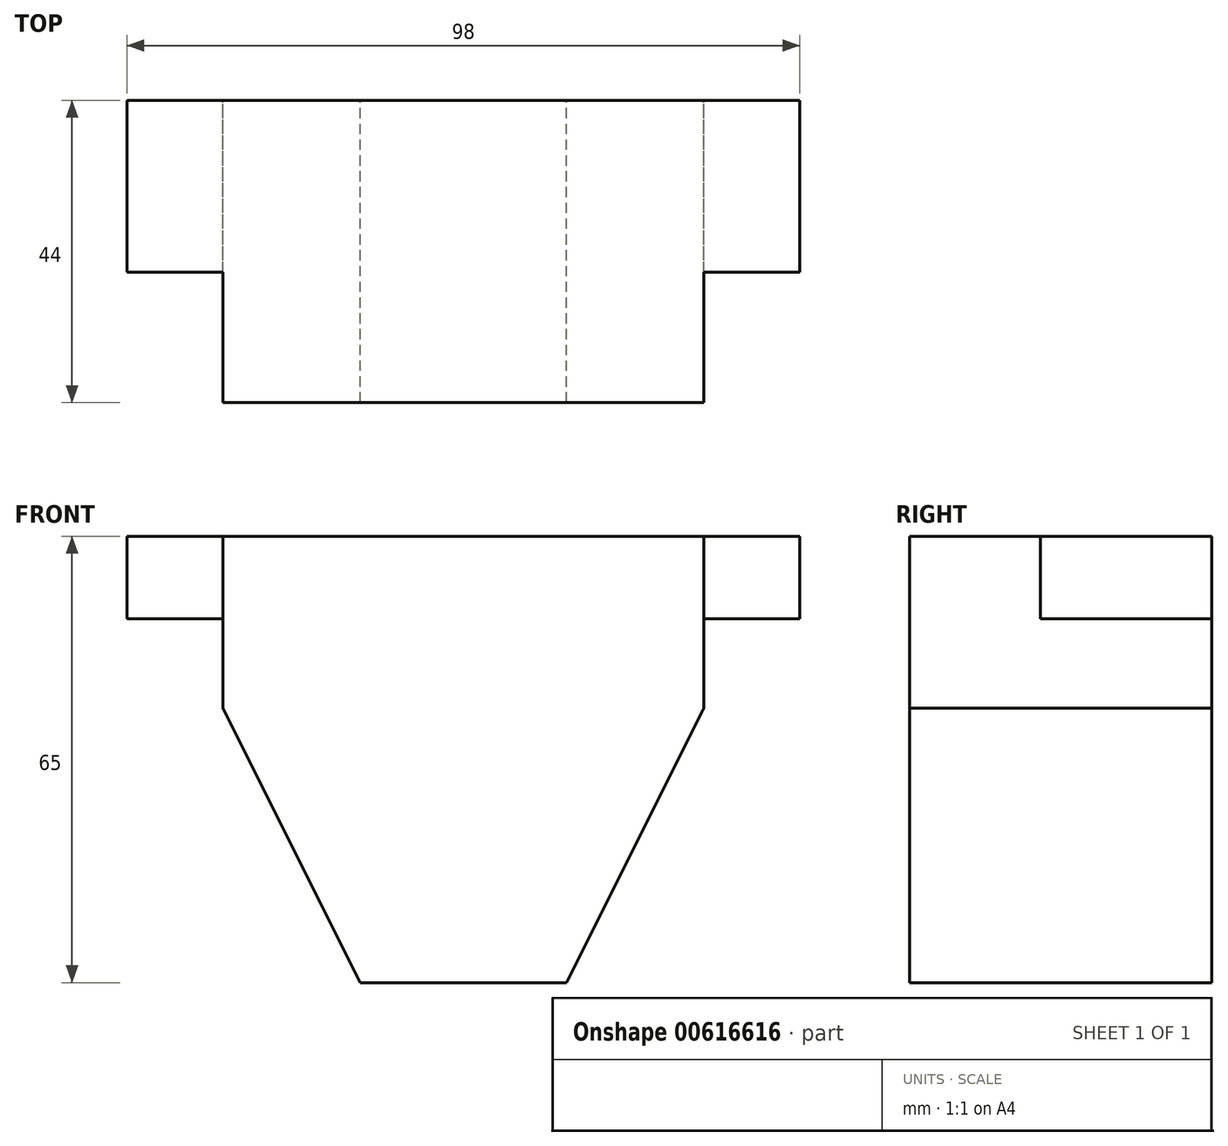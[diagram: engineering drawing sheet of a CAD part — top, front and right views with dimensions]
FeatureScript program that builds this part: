
annotation { "Feature Type Name" : "Feature", "Feature Type Description" : "" }
export const myFeature = defineFeature(function(context is Context, id is Id, definition is map)
    precondition{}
    {
        {
            var Q0;
            Q0=qCreatedBy(makeId("Front.planeOp"),FACE);
            var sketch = newSketch(context, id + "F0", { "sketchPlane" : qUnion([Q0])});
            skLineSegment(sketch, "E0.bottom", {"start": v(-18.65, 25) * mm, "end": v(51.35, 25) * mm});
            skLineSegment(sketch, "E0.top", {"start": v(1.35, -40) * mm, "end": v(31.35, -40) * mm});
            skLineSegment(sketch, "E0.left", {"start": v(-18.65, 25) * mm, "end": v(-18.65, 0) * mm});
            skLineSegment(sketch, "E0.right", {"start": v(51.35, 25) * mm, "end": v(51.35, 0) * mm});
            skLineSegment(sketch, "E1", {"start": v(-18.65, 25) * mm, "end": v(-32.65, 25) * mm});
            skLineSegment(sketch, "E2", {"start": v(-32.65, 25) * mm, "end": v(-32.65, 13) * mm});
            skLineSegment(sketch, "E3", {"start": v(-32.65, 13) * mm, "end": v(-18.65, 13) * mm});
            skLineSegment(sketch, "E4", {"start": v(51.35, 25) * mm, "end": v(65.35, 25) * mm});
            skLineSegment(sketch, "E5", {"start": v(65.35, 25) * mm, "end": v(65.35, 13) * mm});
            skLineSegment(sketch, "E6", {"start": v(51.35, 13) * mm, "end": v(65.35, 13) * mm});
            skLineSegment(sketch, "E7", {"start": v(-18.65, 0) * mm, "end": v(1.35, -40) * mm});
            skLineSegment(sketch, "E8", {"start": v(51.35, 0) * mm, "end": v(31.35, -40) * mm});
            skSolve(sketch);
        }
        {
            var Q0;
            {var subQ3=sQuery(id+"F0.wireOp",EDGE,"E0.bottom");Q0=makeQuery(id+"F0.imprint","IMPRINT",FACE,{"disambiguationData":[TD([[makeQuery(id+"F0.imprint","IMPRINT",EDGE,{"derivedFrom":subQ3}),-1.0]])]});}
            extrude(context, id + "F1", {"entities" : qUnion([Q0]), "depth" : 44 * mm, "offsetDistance" : 25 * mm});
        }
        {
            var Q0;
            {var subQ0=sQuery(id+"F0.wireOp",EDGE,"E1");Q0=makeQuery(id+"F0.imprint","IMPRINT",FACE,{"disambiguationData":[TD([[makeQuery(id+"F0.imprint","IMPRINT",EDGE,{"derivedFrom":subQ0}),1.0]])]});}
            var Q1;
            {var subQ0=sQuery(id+"F0.wireOp",EDGE,"E4");Q1=makeQuery(id+"F0.imprint","IMPRINT",FACE,{"disambiguationData":[TD([[makeQuery(id+"F0.imprint","IMPRINT",EDGE,{"derivedFrom":subQ0}),-1.0]])]});}
            extrude(context, id + "F2", {"entities" : qUnion([Q0, Q1]), "operationType" : NewBodyOperationType.ADD, "depth" : 25 * mm, "offsetDistance" : 25 * mm});
        }
    });
